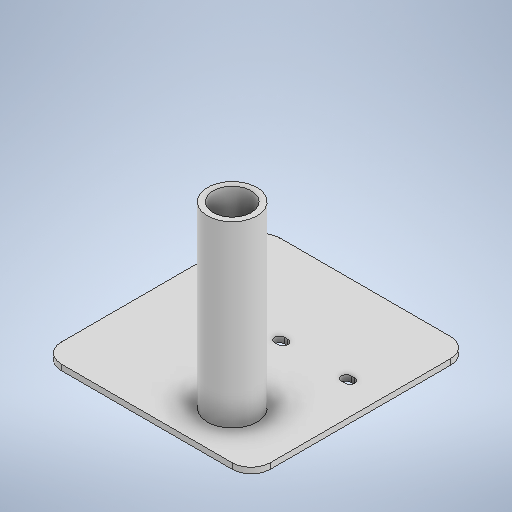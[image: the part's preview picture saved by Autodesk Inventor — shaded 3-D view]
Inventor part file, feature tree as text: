
AUTODESK INVENTOR PART (.ipt)
format: ipt  version: 2025.2 (Build 292293000, 293)  size: 306,688 bytes
history: native  units: mm
features: sketch x8, extrude x7, thread x1, fillet x1
ambient origin geometry x8: Origin, YZ Plane, XZ Plane, XY Plane, X Axis, Y Axis, Z Axis, Center Point
bodies: Solid1 (feature_tree)
feature tree (17):
  extrude  "Extrusion1"  Depth=95.0mm
  extrude  "Extrusion6"  Depth=3.0mm
  extrude  "Extrusion7"  Depth=53.4mm
  sketch  "Sketch8"  dims[d48=5.0mm d49=2.0mm]
  extrude  "Extrusion9"  Depth=5.0mm
  extrude  "Extrusion10"  Depth=2.0mm
  extrude  "Extrusion11"  Depth=5.0mm
  extrude  "Extrusion12"  TaperAngle=0.0deg  [1 undecoded]
  thread  "Thread1"  [1 undecoded]
  fillet  "Fillet2"  [1 undecoded]
  sketch  "Sketch1"  dims[d0=150.0mm d1=95.0mm]
  sketch  "Sketch6"  dims[d41=43.2mm d42=53.4mm]
  sketch  "Sketch7"  dims[d46=37.3mm d47=5.0mm]
  sketch  "Sketch Circular Pattern1"  dims[d2=3.0mm d3=0.0mm d40=25.0mm]
  sketch  "Sketch9"  dims[d50=2.0mm d51=5.0mm]
  sketch  "Sketch10"  dims[d52=5.0mm d53=0.0mm d54=0.0mm d55=40.0mm d56=0.0mm d57=0.0mm]
  sketch  "Sketch11"  dims[d60=90.0mm d62=26.0mm d63=20.0mm d64=3.0mm d65=60.0mm d67=360.0deg d69=20.0mm d73=20.0mm d74=0.0mm d75=94.0mm d76=0.0mm d77=2.0mm d78=0.0mm d79=0.0mm d80=4.0mm d81=5.0mm d82=0.0mm d83=5.0mm d84=0.0mm d85=10.0mm d26=0.5mm d27=0.872665mm d28=0.5mm d29=0.872665mm]
note: 3 required parameter values undecoded (feature->parameter linkage not recoverable at this tier; creation-order binding heuristic only, values carry confidence <= 0.55)
